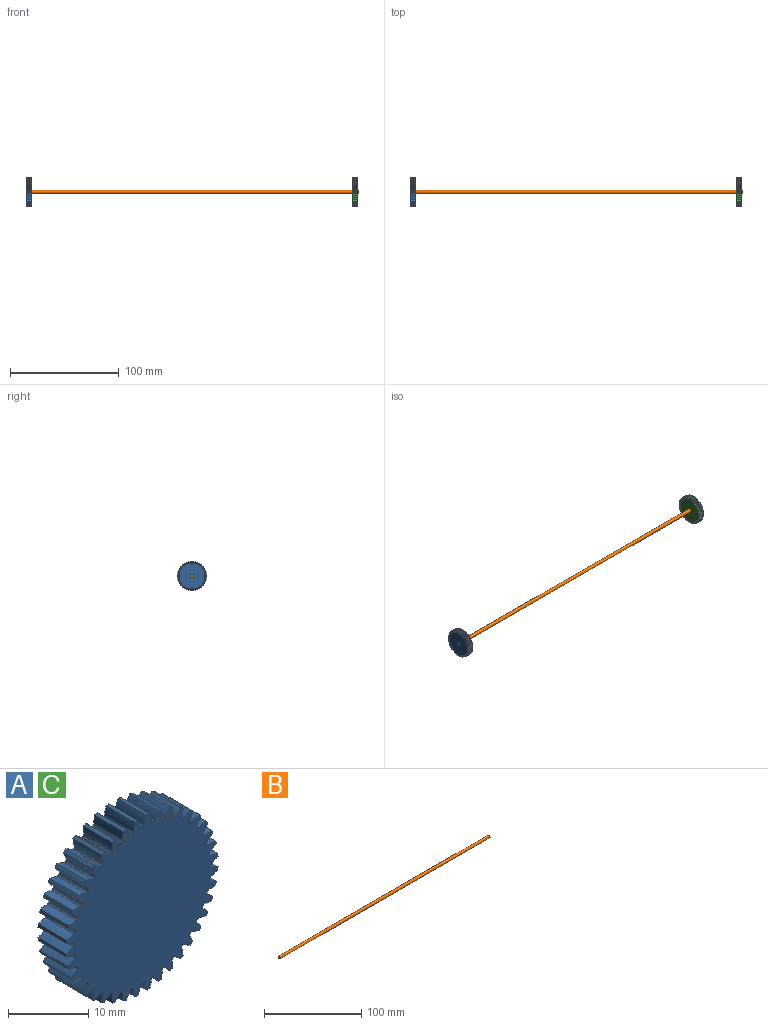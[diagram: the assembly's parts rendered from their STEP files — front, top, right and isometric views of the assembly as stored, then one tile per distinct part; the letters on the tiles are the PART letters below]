
ASSEMBLY  parts=3 mates=2
PART A: 242 faces, bbox 26.6x5.1x26.6 mm
  f0: cylinder r=13.33mm len=5.08mm, axis (0,1,0), area 2.5mm2, adj f39,f41,f147,f239
  f1: cylinder r=13.33mm len=5.08mm, axis (0,1,0), area 2.5mm2, adj f39,f41,f234,f237
  f2: cylinder r=13.33mm len=5.08mm, axis (0,1,0), area 2.5mm2, adj f39,f41,f229,f232
  f3: cylinder r=13.33mm len=5.08mm, axis (0,1,0), area 2.5mm2, adj f39,f41,f224,f227
  f4: cylinder r=13.33mm len=5.08mm, axis (0,1,0), area 2.5mm2, adj f39,f41,f219,f222
  f5: cylinder r=13.33mm len=5.08mm, axis (0,1,0), area 2.5mm2, adj f39,f41,f214,f217
  f6: cylinder r=13.33mm len=5.08mm, axis (0,1,0), area 2.5mm2, adj f39,f41,f209,f212
  f7: cylinder r=13.33mm len=5.08mm, axis (0,1,0), area 2.5mm2, adj f39,f41,f204,f207
  f8: cylinder r=13.33mm len=5.08mm, axis (0,1,0), area 2.5mm2, adj f39,f41,f192,f199
  f9: cylinder r=13.33mm len=5.08mm, axis (0,1,0), area 2.5mm2, adj f39,f41,f194,f202
  f10: cylinder r=13.33mm len=5.08mm, axis (0,1,0), area 2.5mm2, adj f39,f41,f189,f197
  f11: cylinder r=13.33mm len=5.08mm, axis (0,1,0), area 2.5mm2, adj f39,f41,f184,f187
  f12: cylinder r=13.33mm len=5.08mm, axis (0,1,0), area 2.5mm2, adj f39,f41,f179,f182
  f13: cylinder r=13.33mm len=5.08mm, axis (0,1,0), area 2.5mm2, adj f39,f41,f174,f177
  f14: cylinder r=13.33mm len=5.08mm, axis (0,1,0), area 2.5mm2, adj f39,f41,f169,f172
  f15: cylinder r=13.33mm len=5.08mm, axis (0,1,0), area 2.5mm2, adj f39,f41,f164,f167
  f16: cylinder r=13.33mm len=5.08mm, axis (0,1,0), area 2.5mm2, adj f39,f41,f137,f159
  f17: cylinder r=13.33mm len=5.08mm, axis (0,1,0), area 2.5mm2, adj f39,f41,f154,f157
  f18: cylinder r=13.33mm len=5.08mm, axis (0,1,0), area 2.5mm2, adj f39,f41,f142,f149
  f19: cylinder r=13.33mm len=5.08mm, axis (0,1,0), area 2.5mm2, adj f39,f41,f144,f152
  f20: cylinder r=13.33mm len=5.08mm, axis (0,1,0), area 2.5mm2, adj f39,f41,f132,f139
  f21: cylinder r=13.33mm len=5.08mm, axis (0,1,0), area 2.5mm2, adj f39,f41,f127,f134
  f22: cylinder r=13.33mm len=5.08mm, axis (0,1,0), area 2.5mm2, adj f39,f41,f122,f129
  f23: cylinder r=13.33mm len=5.08mm, axis (0,1,0), area 2.5mm2, adj f39,f41,f82,f124
  f24: cylinder r=13.33mm len=5.08mm, axis (0,1,0), area 2.5mm2, adj f39,f41,f42,f119
  f25: cylinder r=13.33mm len=5.08mm, axis (0,1,0), area 2.5mm2, adj f39,f41,f114,f117
  f26: cylinder r=13.33mm len=5.08mm, axis (0,1,0), area 2.5mm2, adj f39,f41,f109,f112
  f27: cylinder r=13.33mm len=5.08mm, axis (0,1,0), area 2.5mm2, adj f39,f41,f104,f107
  f28: cylinder r=13.33mm len=5.08mm, axis (0,1,0), area 2.5mm2, adj f39,f41,f92,f99
  f29: cylinder r=13.33mm len=5.08mm, axis (0,1,0), area 2.5mm2, adj f39,f41,f94,f102
  f30: cylinder r=13.33mm len=5.08mm, axis (0,1,0), area 2.5mm2, adj f39,f41,f89,f97
  f31: cylinder r=13.33mm len=5.08mm, axis (0,1,0), area 2.5mm2, adj f39,f41,f84,f87
  f32: cylinder r=13.33mm len=5.08mm, axis (0,1,0), area 2.5mm2, adj f39,f41,f67,f79
  f33: cylinder r=13.33mm len=5.08mm, axis (0,1,0), area 2.5mm2, adj f39,f41,f74,f77
  f34: cylinder r=13.33mm len=5.08mm, axis (0,1,0), area 2.5mm2, adj f39,f41,f62,f69
  f35: cylinder r=13.33mm len=5.08mm, axis (0,1,0), area 2.5mm2, adj f39,f41,f64,f162
  f36: cylinder r=13.33mm len=5.08mm, axis (0,1,0), area 2.5mm2, adj f39,f41,f59,f72
  f37: cylinder r=13.33mm len=5.08mm, axis (0,1,0), area 2.5mm2, adj f39,f41,f54,f57
  f38: cylinder r=13.33mm len=5.08mm, axis (0,1,0), area 2.5mm2, adj f39,f41,f49,f52
  f39: plane 26.62x26.62mm, normal (0,-1,0), area 502.9mm2, adj f0,f1,f2,f3,f4,f5,f6,f7
  f40: cylinder r=13.33mm len=5.08mm, axis (0,1,0), area 2.5mm2, adj f39,f41,f44,f47
  f41: plane 26.62x26.62mm, normal (0,1,0), area 502.9mm2, adj f0,f1,f2,f3,f4,f5,f6,f7
  f42: extruded ~5.08x1.22mm, area 6.7mm2, adj f24,f39,f41,f45
  f43: cylinder r=11.91mm len=5.08mm, axis (0,1,0), area 0.9mm2, adj f39,f41,f45,f46
  f44: extruded ~5.08x1.22mm, area 6.7mm2, adj f39,f40,f41,f46
  f45: cylinder r=0.22mm len=5.08mm, axis (0,1,0), area 1.6mm2, adj f39,f41,f42,f43
  f46: cylinder r=0.22mm len=5.08mm, axis (0,1,0), area 1.6mm2, adj f39,f41,f43,f44
  f47: extruded ~5.08x1.28mm, area 6.7mm2, adj f39,f40,f41,f50
  f48: cylinder r=11.91mm len=5.08mm, axis (0,1,0), area 0.9mm2, adj f39,f41,f50,f51
  f49: extruded ~5.08x1.13mm, area 6.7mm2, adj f38,f39,f41,f51
  f50: cylinder r=0.22mm len=5.08mm, axis (0,1,0), area 1.6mm2, adj f39,f41,f47,f48
  f51: cylinder r=0.22mm len=5.08mm, axis (0,1,0), area 1.6mm2, adj f39,f41,f48,f49
  f52: extruded ~5.08x1.31mm, area 6.7mm2, adj f38,f39,f41,f55
  f53: cylinder r=11.91mm len=5.08mm, axis (0,1,0), area 0.9mm2, adj f39,f41,f55,f56
  f54: extruded ~5.08x1.01mm, area 6.7mm2, adj f37,f39,f41,f56
  f55: cylinder r=0.22mm len=5.08mm, axis (0,1,0), area 1.6mm2, adj f39,f41,f52,f53
  f56: cylinder r=0.22mm len=5.08mm, axis (0,1,0), area 1.6mm2, adj f39,f41,f53,f54
  f57: extruded ~5.08x1.31mm, area 6.7mm2, adj f37,f39,f41,f60
  f58: cylinder r=11.91mm len=5.08mm, axis (0,1,0), area 0.9mm2, adj f39,f41,f60,f61
  f59: extruded ~5.08x0.99mm, area 6.7mm2, adj f36,f39,f41,f61
  f60: cylinder r=0.22mm len=5.08mm, axis (0,1,0), area 1.6mm2, adj f39,f41,f57,f58
  f61: cylinder r=0.22mm len=5.08mm, axis (0,1,0), area 1.6mm2, adj f39,f41,f58,f59
  f62: extruded ~5.08x0.99mm, area 6.7mm2, adj f34,f39,f41,f65
  f63: cylinder r=11.91mm len=5.08mm, axis (0,1,0), area 0.9mm2, adj f39,f41,f65,f66
  f64: extruded ~5.08x1.31mm, area 6.7mm2, adj f35,f39,f41,f66
  f65: cylinder r=0.22mm len=5.08mm, axis (0,1,0), area 1.6mm2, adj f39,f41,f62,f63
  f66: cylinder r=0.22mm len=5.08mm, axis (0,1,0), area 1.6mm2, adj f39,f41,f63,f64
  f67: extruded ~5.08x1.12mm, area 6.7mm2, adj f32,f39,f41,f70
  f68: cylinder r=11.91mm len=5.08mm, axis (0,1,0), area 0.9mm2, adj f39,f41,f70,f71
  f69: extruded ~5.08x1.28mm, area 6.7mm2, adj f34,f39,f41,f71
  f70: cylinder r=0.22mm len=5.08mm, axis (0,1,0), area 1.6mm2, adj f39,f41,f67,f68
  f71: cylinder r=0.22mm len=5.08mm, axis (0,1,0), area 1.6mm2, adj f39,f41,f68,f69
  f72: extruded ~5.08x1.28mm, area 6.7mm2, adj f36,f39,f41,f75
  f73: cylinder r=11.91mm len=5.08mm, axis (0,1,0), area 0.9mm2, adj f39,f41,f75,f76
  f74: extruded ~5.08x1.12mm, area 6.7mm2, adj f33,f39,f41,f76
  f75: cylinder r=0.22mm len=5.08mm, axis (0,1,0), area 1.6mm2, adj f39,f41,f72,f73
  f76: cylinder r=0.22mm len=5.08mm, axis (0,1,0), area 1.6mm2, adj f39,f41,f73,f74
  f77: extruded ~5.08x1.21mm, area 6.7mm2, adj f33,f39,f41,f80
  f78: cylinder r=11.91mm len=5.08mm, axis (0,1,0), area 0.9mm2, adj f39,f41,f80,f81
  f79: extruded ~5.08x1.21mm, area 6.7mm2, adj f32,f39,f41,f81
  f80: cylinder r=0.22mm len=5.08mm, axis (0,1,0), area 1.6mm2, adj f39,f41,f77,f78
  f81: cylinder r=0.22mm len=5.08mm, axis (0,1,0), area 1.6mm2, adj f39,f41,f78,f79
  f82: extruded ~5.08x1.31mm, area 6.7mm2, adj f23,f39,f41,f85
  f83: cylinder r=11.91mm len=5.08mm, axis (0,1,0), area 0.9mm2, adj f39,f41,f85,f86
  f84: extruded ~5.08x1.01mm, area 6.7mm2, adj f31,f39,f41,f86
  f85: cylinder r=0.22mm len=5.08mm, axis (0,1,0), area 1.6mm2, adj f39,f41,f82,f83
  f86: cylinder r=0.22mm len=5.08mm, axis (0,1,0), area 1.6mm2, adj f39,f41,f83,f84
  f87: extruded ~5.08x1.31mm, area 6.7mm2, adj f31,f39,f41,f90
  f88: cylinder r=11.91mm len=5.08mm, axis (0,1,0), area 0.9mm2, adj f39,f41,f90,f91
  f89: extruded ~5.08x0.99mm, area 6.7mm2, adj f30,f39,f41,f91
  f90: cylinder r=0.22mm len=5.08mm, axis (0,1,0), area 1.6mm2, adj f39,f41,f87,f88
  f91: cylinder r=0.22mm len=5.08mm, axis (0,1,0), area 1.6mm2, adj f39,f41,f88,f89
  f92: extruded ~5.08x1.21mm, area 6.7mm2, adj f28,f39,f41,f95
  f93: cylinder r=11.91mm len=5.08mm, axis (0,1,0), area 0.9mm2, adj f39,f41,f95,f96
  f94: extruded ~5.08x1.21mm, area 6.7mm2, adj f29,f39,f41,f96
  f95: cylinder r=0.22mm len=5.08mm, axis (0,1,0), area 1.6mm2, adj f39,f41,f92,f93
  f96: cylinder r=0.22mm len=5.08mm, axis (0,1,0), area 1.6mm2, adj f39,f41,f93,f94
  f97: extruded ~5.08x1.28mm, area 6.7mm2, adj f30,f39,f41,f100
  f98: cylinder r=11.91mm len=5.08mm, axis (0,1,0), area 0.9mm2, adj f39,f41,f100,f101
  f99: extruded ~5.08x1.12mm, area 6.7mm2, adj f28,f39,f41,f101
  f100: cylinder r=0.22mm len=5.08mm, axis (0,1,0), area 1.6mm2, adj f39,f41,f97,f98
  f101: cylinder r=0.22mm len=5.08mm, axis (0,1,0), area 1.6mm2, adj f39,f41,f98,f99
  f102: extruded ~5.08x1.12mm, area 6.7mm2, adj f29,f39,f41,f105
  f103: cylinder r=11.91mm len=5.08mm, axis (0,1,0), area 0.9mm2, adj f39,f41,f105,f106
  f104: extruded ~5.08x1.28mm, area 6.7mm2, adj f27,f39,f41,f106
  f105: cylinder r=0.22mm len=5.08mm, axis (0,1,0), area 1.6mm2, adj f39,f41,f102,f103
  f106: cylinder r=0.22mm len=5.08mm, axis (0,1,0), area 1.6mm2, adj f39,f41,f103,f104
  f107: extruded ~5.08x0.99mm, area 6.7mm2, adj f27,f39,f41,f110
  f108: cylinder r=11.91mm len=5.08mm, axis (0,1,0), area 0.9mm2, adj f39,f41,f110,f111
  f109: extruded ~5.08x1.31mm, area 6.7mm2, adj f26,f39,f41,f111
  f110: cylinder r=0.22mm len=5.08mm, axis (0,1,0), area 1.6mm2, adj f39,f41,f107,f108
  f111: cylinder r=0.22mm len=5.08mm, axis (0,1,0), area 1.6mm2, adj f39,f41,f108,f109
  f112: extruded ~5.08x1.01mm, area 6.7mm2, adj f26,f39,f41,f115
  f113: cylinder r=11.91mm len=5.08mm, axis (0,1,0), area 0.9mm2, adj f39,f41,f115,f116
  f114: extruded ~5.08x1.31mm, area 6.7mm2, adj f25,f39,f41,f116
  f115: cylinder r=0.22mm len=5.08mm, axis (0,1,0), area 1.6mm2, adj f39,f41,f112,f113
  f116: cylinder r=0.22mm len=5.08mm, axis (0,1,0), area 1.6mm2, adj f39,f41,f113,f114
  f117: extruded ~5.08x1.13mm, area 6.7mm2, adj f25,f39,f41,f120
  f118: cylinder r=11.91mm len=5.08mm, axis (0,1,0), area 0.9mm2, adj f39,f41,f120,f121
  f119: extruded ~5.08x1.28mm, area 6.7mm2, adj f24,f39,f41,f121
  f120: cylinder r=0.22mm len=5.08mm, axis (0,1,0), area 1.6mm2, adj f39,f41,f117,f118
  f121: cylinder r=0.22mm len=5.08mm, axis (0,1,0), area 1.6mm2, adj f39,f41,f118,f119
  f122: extruded ~5.08x1.28mm, area 6.7mm2, adj f22,f39,f41,f125
  f123: cylinder r=11.91mm len=5.08mm, axis (0,1,0), area 0.9mm2, adj f39,f41,f125,f126
  f124: extruded ~5.08x1.13mm, area 6.7mm2, adj f23,f39,f41,f126
  f125: cylinder r=0.22mm len=5.08mm, axis (0,1,0), area 1.6mm2, adj f39,f41,f122,f123
  f126: cylinder r=0.22mm len=5.08mm, axis (0,1,0), area 1.6mm2, adj f39,f41,f123,f124
  f127: extruded ~5.08x1.22mm, area 6.7mm2, adj f21,f39,f41,f130
  f128: cylinder r=11.91mm len=5.08mm, axis (0,1,0), area 0.9mm2, adj f39,f41,f130,f131
  f129: extruded ~5.08x1.22mm, area 6.7mm2, adj f22,f39,f41,f131
  f130: cylinder r=0.22mm len=5.08mm, axis (0,1,0), area 1.6mm2, adj f39,f41,f127,f128
  f131: cylinder r=0.22mm len=5.08mm, axis (0,1,0), area 1.6mm2, adj f39,f41,f128,f129
  f132: extruded ~5.08x1.13mm, area 6.7mm2, adj f20,f39,f41,f135
  f133: cylinder r=11.91mm len=5.08mm, axis (0,1,0), area 0.9mm2, adj f39,f41,f135,f136
  f134: extruded ~5.08x1.28mm, area 6.7mm2, adj f21,f39,f41,f136
  f135: cylinder r=0.22mm len=5.08mm, axis (0,1,0), area 1.6mm2, adj f39,f41,f132,f133
  f136: cylinder r=0.22mm len=5.08mm, axis (0,1,0), area 1.6mm2, adj f39,f41,f133,f134
  f137: extruded ~5.08x1.01mm, area 6.7mm2, adj f16,f39,f41,f140
  f138: cylinder r=11.91mm len=5.08mm, axis (0,1,0), area 0.9mm2, adj f39,f41,f140,f141
  f139: extruded ~5.08x1.31mm, area 6.7mm2, adj f20,f39,f41,f141
  f140: cylinder r=0.22mm len=5.08mm, axis (0,1,0), area 1.6mm2, adj f39,f41,f137,f138
  f141: cylinder r=0.22mm len=5.08mm, axis (0,1,0), area 1.6mm2, adj f39,f41,f138,f139
  f142: extruded ~5.08x1.21mm, area 6.7mm2, adj f18,f39,f41,f145
  f143: cylinder r=11.91mm len=5.08mm, axis (0,1,0), area 0.9mm2, adj f39,f41,f145,f146
  f144: extruded ~5.08x1.21mm, area 6.7mm2, adj f19,f39,f41,f146
  f145: cylinder r=0.22mm len=5.08mm, axis (0,1,0), area 1.6mm2, adj f39,f41,f142,f143
  f146: cylinder r=0.22mm len=5.08mm, axis (0,1,0), area 1.6mm2, adj f39,f41,f143,f144
  f147: extruded ~5.08x1.28mm, area 6.7mm2, adj f0,f39,f41,f150
  f148: cylinder r=11.91mm len=5.08mm, axis (0,1,0), area 0.9mm2, adj f39,f41,f150,f151
  f149: extruded ~5.08x1.12mm, area 6.7mm2, adj f18,f39,f41,f151
  f150: cylinder r=0.22mm len=5.08mm, axis (0,1,0), area 1.6mm2, adj f39,f41,f147,f148
  f151: cylinder r=0.22mm len=5.08mm, axis (0,1,0), area 1.6mm2, adj f39,f41,f148,f149
  f152: extruded ~5.08x1.12mm, area 6.7mm2, adj f19,f39,f41,f155
  f153: cylinder r=11.91mm len=5.08mm, axis (0,1,0), area 0.9mm2, adj f39,f41,f155,f156
  f154: extruded ~5.08x1.28mm, area 6.7mm2, adj f17,f39,f41,f156
  f155: cylinder r=0.22mm len=5.08mm, axis (0,1,0), area 1.6mm2, adj f39,f41,f152,f153
  f156: cylinder r=0.22mm len=5.08mm, axis (0,1,0), area 1.6mm2, adj f39,f41,f153,f154
  f157: extruded ~5.08x0.99mm, area 6.7mm2, adj f17,f39,f41,f160
  f158: cylinder r=11.91mm len=5.08mm, axis (0,1,0), area 0.9mm2, adj f39,f41,f160,f161
  f159: extruded ~5.08x1.31mm, area 6.7mm2, adj f16,f39,f41,f161
  f160: cylinder r=0.22mm len=5.08mm, axis (0,1,0), area 1.6mm2, adj f39,f41,f157,f158
  f161: cylinder r=0.22mm len=5.08mm, axis (0,1,0), area 1.6mm2, adj f39,f41,f158,f159
  f162: extruded ~5.08x1.01mm, area 6.7mm2, adj f35,f39,f41,f165
  f163: cylinder r=11.91mm len=5.08mm, axis (0,1,0), area 0.9mm2, adj f39,f41,f165,f166
  f164: extruded ~5.08x1.31mm, area 6.7mm2, adj f15,f39,f41,f166
  f165: cylinder r=0.22mm len=5.08mm, axis (0,1,0), area 1.6mm2, adj f39,f41,f162,f163
  f166: cylinder r=0.22mm len=5.08mm, axis (0,1,0), area 1.6mm2, adj f39,f41,f163,f164
  f167: extruded ~5.08x1.13mm, area 6.7mm2, adj f15,f39,f41,f170
  f168: cylinder r=11.91mm len=5.08mm, axis (0,1,0), area 0.9mm2, adj f39,f41,f170,f171
  f169: extruded ~5.08x1.28mm, area 6.7mm2, adj f14,f39,f41,f171
  f170: cylinder r=0.22mm len=5.08mm, axis (0,1,0), area 1.6mm2, adj f39,f41,f167,f168
  f171: cylinder r=0.22mm len=5.08mm, axis (0,1,0), area 1.6mm2, adj f39,f41,f168,f169
  f172: extruded ~5.08x1.22mm, area 6.7mm2, adj f14,f39,f41,f175
  f173: cylinder r=11.91mm len=5.08mm, axis (0,1,0), area 0.9mm2, adj f39,f41,f175,f176
  f174: extruded ~5.08x1.22mm, area 6.7mm2, adj f13,f39,f41,f176
  f175: cylinder r=0.22mm len=5.08mm, axis (0,1,0), area 1.6mm2, adj f39,f41,f172,f173
  f176: cylinder r=0.22mm len=5.08mm, axis (0,1,0), area 1.6mm2, adj f39,f41,f173,f174
  f177: extruded ~5.08x1.28mm, area 6.7mm2, adj f13,f39,f41,f180
  f178: cylinder r=11.91mm len=5.08mm, axis (0,1,0), area 0.9mm2, adj f39,f41,f180,f181
  f179: extruded ~5.08x1.13mm, area 6.7mm2, adj f12,f39,f41,f181
  f180: cylinder r=0.22mm len=5.08mm, axis (0,1,0), area 1.6mm2, adj f39,f41,f177,f178
  f181: cylinder r=0.22mm len=5.08mm, axis (0,1,0), area 1.6mm2, adj f39,f41,f178,f179
  f182: extruded ~5.08x1.31mm, area 6.7mm2, adj f12,f39,f41,f185
  f183: cylinder r=11.91mm len=5.08mm, axis (0,1,0), area 0.9mm2, adj f39,f41,f185,f186
  f184: extruded ~5.08x1.01mm, area 6.7mm2, adj f11,f39,f41,f186
  f185: cylinder r=0.22mm len=5.08mm, axis (0,1,0), area 1.6mm2, adj f39,f41,f182,f183
  f186: cylinder r=0.22mm len=5.08mm, axis (0,1,0), area 1.6mm2, adj f39,f41,f183,f184
  f187: extruded ~5.08x1.31mm, area 6.7mm2, adj f11,f39,f41,f190
  f188: cylinder r=11.91mm len=5.08mm, axis (0,1,0), area 0.9mm2, adj f39,f41,f190,f191
  f189: extruded ~5.08x0.99mm, area 6.7mm2, adj f10,f39,f41,f191
  f190: cylinder r=0.22mm len=5.08mm, axis (0,1,0), area 1.6mm2, adj f39,f41,f187,f188
  f191: cylinder r=0.22mm len=5.08mm, axis (0,1,0), area 1.6mm2, adj f39,f41,f188,f189
  f192: extruded ~5.08x1.21mm, area 6.7mm2, adj f8,f39,f41,f195
  f193: cylinder r=11.91mm len=5.08mm, axis (0,1,0), area 0.9mm2, adj f39,f41,f195,f196
  f194: extruded ~5.08x1.21mm, area 6.7mm2, adj f9,f39,f41,f196
  f195: cylinder r=0.22mm len=5.08mm, axis (0,1,0), area 1.6mm2, adj f39,f41,f192,f193
  f196: cylinder r=0.22mm len=5.08mm, axis (0,1,0), area 1.6mm2, adj f39,f41,f193,f194
  f197: extruded ~5.08x1.28mm, area 6.7mm2, adj f10,f39,f41,f200
  f198: cylinder r=11.91mm len=5.08mm, axis (0,1,0), area 0.9mm2, adj f39,f41,f200,f201
  f199: extruded ~5.08x1.12mm, area 6.7mm2, adj f8,f39,f41,f201
  f200: cylinder r=0.22mm len=5.08mm, axis (0,1,0), area 1.6mm2, adj f39,f41,f197,f198
  f201: cylinder r=0.22mm len=5.08mm, axis (0,1,0), area 1.6mm2, adj f39,f41,f198,f199
  f202: extruded ~5.08x1.12mm, area 6.7mm2, adj f9,f39,f41,f205
  f203: cylinder r=11.91mm len=5.08mm, axis (0,1,0), area 0.9mm2, adj f39,f41,f205,f206
  f204: extruded ~5.08x1.28mm, area 6.7mm2, adj f7,f39,f41,f206
  f205: cylinder r=0.22mm len=5.08mm, axis (0,1,0), area 1.6mm2, adj f39,f41,f202,f203
  f206: cylinder r=0.22mm len=5.08mm, axis (0,1,0), area 1.6mm2, adj f39,f41,f203,f204
  f207: extruded ~5.08x0.99mm, area 6.7mm2, adj f7,f39,f41,f210
  f208: cylinder r=11.91mm len=5.08mm, axis (0,1,0), area 0.9mm2, adj f39,f41,f210,f211
  f209: extruded ~5.08x1.31mm, area 6.7mm2, adj f6,f39,f41,f211
  f210: cylinder r=0.22mm len=5.08mm, axis (0,1,0), area 1.6mm2, adj f39,f41,f207,f208
  f211: cylinder r=0.22mm len=5.08mm, axis (0,1,0), area 1.6mm2, adj f39,f41,f208,f209
  f212: extruded ~5.08x1.01mm, area 6.7mm2, adj f6,f39,f41,f215
  f213: cylinder r=11.91mm len=5.08mm, axis (0,1,0), area 0.9mm2, adj f39,f41,f215,f216
  f214: extruded ~5.08x1.31mm, area 6.7mm2, adj f5,f39,f41,f216
  f215: cylinder r=0.22mm len=5.08mm, axis (0,1,0), area 1.6mm2, adj f39,f41,f212,f213
  f216: cylinder r=0.22mm len=5.08mm, axis (0,1,0), area 1.6mm2, adj f39,f41,f213,f214
  f217: extruded ~5.08x1.13mm, area 6.7mm2, adj f5,f39,f41,f220
  f218: cylinder r=11.91mm len=5.08mm, axis (0,1,0), area 0.9mm2, adj f39,f41,f220,f221
  f219: extruded ~5.08x1.28mm, area 6.7mm2, adj f4,f39,f41,f221
  f220: cylinder r=0.22mm len=5.08mm, axis (0,1,0), area 1.6mm2, adj f39,f41,f217,f218
  f221: cylinder r=0.22mm len=5.08mm, axis (0,1,0), area 1.6mm2, adj f39,f41,f218,f219
  f222: extruded ~5.08x1.22mm, area 6.7mm2, adj f4,f39,f41,f225
  f223: cylinder r=11.91mm len=5.08mm, axis (0,1,0), area 0.9mm2, adj f39,f41,f225,f226
  f224: extruded ~5.08x1.22mm, area 6.7mm2, adj f3,f39,f41,f226
  f225: cylinder r=0.22mm len=5.08mm, axis (0,1,0), area 1.6mm2, adj f39,f41,f222,f223
  f226: cylinder r=0.22mm len=5.08mm, axis (0,1,0), area 1.6mm2, adj f39,f41,f223,f224
  f227: extruded ~5.08x1.28mm, area 6.7mm2, adj f3,f39,f41,f230
  f228: cylinder r=11.91mm len=5.08mm, axis (0,1,0), area 0.9mm2, adj f39,f41,f230,f231
  f229: extruded ~5.08x1.13mm, area 6.7mm2, adj f2,f39,f41,f231
  f230: cylinder r=0.22mm len=5.08mm, axis (0,1,0), area 1.6mm2, adj f39,f41,f227,f228
  f231: cylinder r=0.22mm len=5.08mm, axis (0,1,0), area 1.6mm2, adj f39,f41,f228,f229
  f232: extruded ~5.08x1.31mm, area 6.7mm2, adj f2,f39,f41,f235
  f233: cylinder r=11.91mm len=5.08mm, axis (0,1,0), area 0.9mm2, adj f39,f41,f235,f236
  f234: extruded ~5.08x1.01mm, area 6.7mm2, adj f1,f39,f41,f236
  f235: cylinder r=0.22mm len=5.08mm, axis (0,1,0), area 1.6mm2, adj f39,f41,f232,f233
  f236: cylinder r=0.22mm len=5.08mm, axis (0,1,0), area 1.6mm2, adj f39,f41,f233,f234
  f237: extruded ~5.08x1.31mm, area 6.7mm2, adj f1,f39,f41,f240
  f238: cylinder r=11.91mm len=5.08mm, axis (0,1,0), area 0.9mm2, adj f39,f41,f240,f241
  f239: extruded ~5.08x0.99mm, area 6.7mm2, adj f0,f39,f41,f241
  f240: cylinder r=0.22mm len=5.08mm, axis (0,1,0), area 1.6mm2, adj f39,f41,f237,f238
  f241: cylinder r=0.22mm len=5.08mm, axis (0,1,0), area 1.6mm2, adj f39,f41,f238,f239
PART B: 3 faces, bbox 304.8x3.2x3.2 mm
  f0: cylinder r=1.59mm len=304.8mm, axis (-1,0,0), area 3040.2mm2, adj f1,f2
  f1: plane 3.18x3.18mm, normal (1,0,0), area 7.9mm2, adj f0
  f2: plane 3.18x3.18mm, normal (-1,0,0), area 7.9mm2, adj f0
PART C: same geometry as A
PLACE A rot(axis=(-0.58,-0.58,-0.58),120deg) t=(5.08,27.88,20.13)mm
PLACE B at identity
PLACE C rot(axis=(-0.58,0.58,0.58),120deg) t=(299.72,27.88,20.13)mm
MATE fastened A.f0 <-> B.f0  axis (-1,0,0) through (0,27.88,20.13)mm
MATE fastened C.f0 <-> B.f0  axis (1,0,0) through (304.8,27.88,20.13)mm
